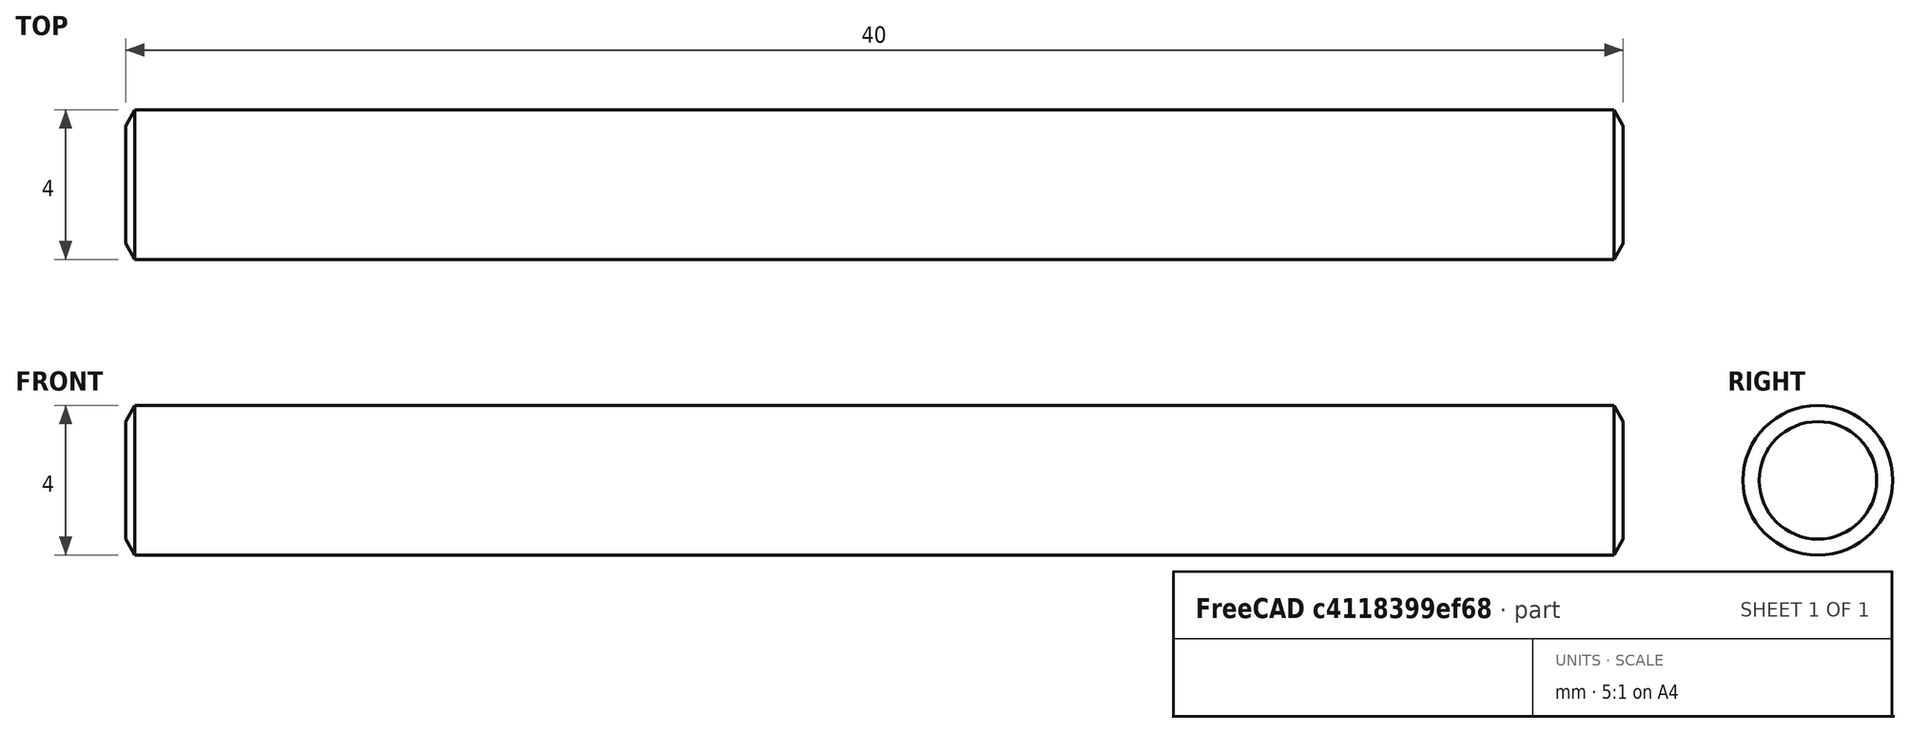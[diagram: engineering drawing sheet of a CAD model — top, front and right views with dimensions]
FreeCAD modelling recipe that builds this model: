
FCSTD DOCUMENT  (FreeCAD 0.14R3700 (Git))
Label: Gewindestange_M4x40
License: CC-BY 3.0
LicenseURL: http://creativecommons.org/licenses/by/3.0/
objects: Sketcher::SketchObject×1, PartDesign::Revolution×1
note: 3 computed .brp shape members not serialized (recipe doc carries the construction recipe); baked Part::Feature solids carry a one-line shape summary decoded from their .brp

FEATURE [Sketcher::SketchObject] Sketch
  Placement = pos=(0,0,0) rot=(1,0,0;1.5708rad)
  sketch-geometry (7):
    g0: LineSegment StartX=0 StartY=0 StartZ=0 EndX=0 EndY=1.57 EndZ=0
    g1: LineSegment StartX=0 StartY=1.57 StartZ=0 EndX=0.248261 EndY=2 EndZ=0
    g2: LineSegment StartX=0.248261 StartY=2 StartZ=0 EndX=39.7517 EndY=2 EndZ=0
    g3: LineSegment StartX=39.7517 StartY=2 StartZ=0 EndX=40 EndY=1.57 EndZ=0
    g4: LineSegment StartX=40 StartY=1.57 StartZ=0 EndX=40 EndY=0 EndZ=0
    g5: LineSegment StartX=40 StartY=0 StartZ=0 EndX=0 EndY=0 EndZ=0
    g6: LineSegment [constr] StartX=0 StartY=1.57 StartZ=0 EndX=40 EndY=1.57 EndZ=0
  constraints (19):
    c: Coincident(g-1,g0)
    c: PointOnObject(g0,g-2)
    c: Coincident(g0,g1)
    c: Coincident(g1,g2)
    c: Horizontal(g2)
    c: Coincident(g2,g3)
    c: Coincident(g3,g4)
    c: Vertical(g4)
    c: Coincident(g4,g5)
    c: Coincident(g5,g0)
    c: Horizontal(g5)
    c: Equal(g1,g3)
    c: Angle(g1,g3) = 1.0472
    c: Coincident(g6,g0)
    c: Coincident(g6,g3)
    c: Horizontal(g6)
    c: DistanceX(g5) = -40
    c: DistanceY(g4) = -1.57
    c: DistanceY(g4,g2) = 2
FEATURE [PartDesign::Revolution] Revolution  label="Gewindestange M4 x 40 #"
  Angle = 360
  Axis = (1,0,0)
  Base = (0,0,0)
  Placement = pos=(0,0,0) rot=(1,0,0;1.5708rad)
  ReferenceAxis = -> Sketch [H_Axis]
  Sketch = -> Sketch
